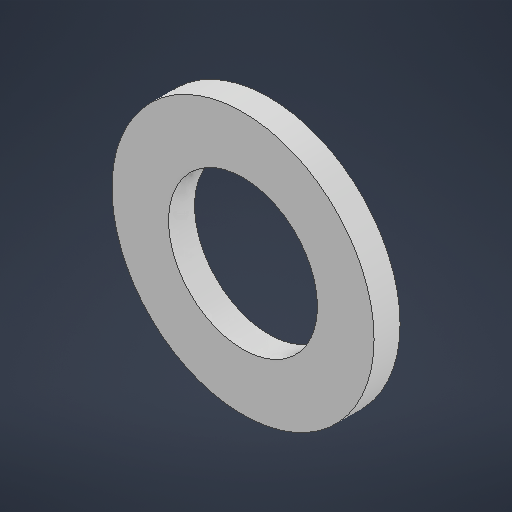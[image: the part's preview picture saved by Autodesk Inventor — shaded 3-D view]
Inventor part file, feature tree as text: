
AUTODESK INVENTOR PART (.ipt)
format: ipt  version: 2025 (Build 290162000, 162)  size: 192,000 bytes
history: native  units: in
note: dims shown in document units (in); Inventor stores cm internally (conversion verified against a paired STEP export)
features: extrude x1
ambient origin geometry x8: Origin, YZ Plane, XZ Plane, XY Plane, X Axis, Y Axis, Z Axis, Center Point
bodies: Solid1 (feature_tree)
feature tree (1):
  extrude  "Extrude1"  [1 undecoded]
note: 1 required parameter value undecoded (feature->parameter linkage not recoverable at this tier; creation-order binding heuristic only, values carry confidence <= 0.55)
